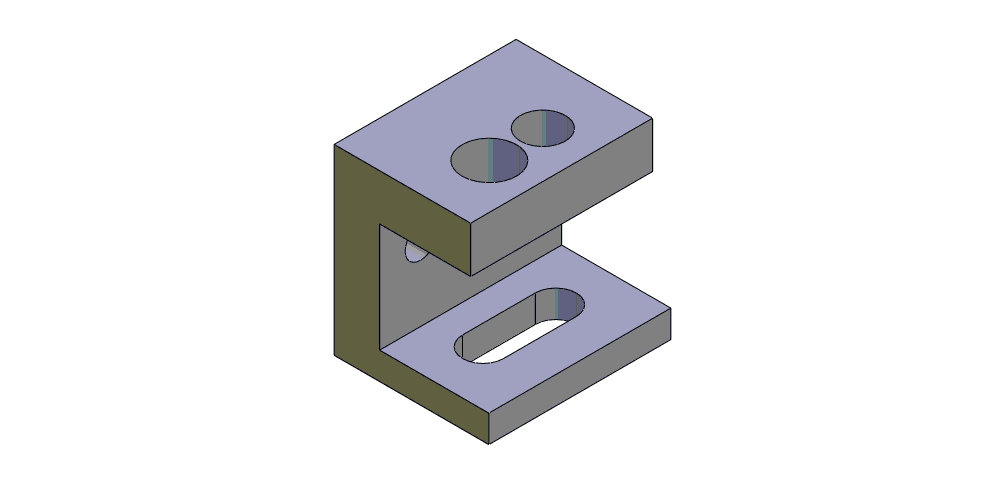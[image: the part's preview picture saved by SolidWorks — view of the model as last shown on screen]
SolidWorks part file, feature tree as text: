
SOLIDWORKS PART (.sldprt)
format: sldprt  version: not decoded by parser v0  size: 209,920 bytes
history: native  units: mm
features: sketch x8, extrude x3, cut_extrude x3, material x1, hole x1 (+12 scaffold rows collapsed)
feature tree (28):
  scaffold x12  (default folders/planes/origin — collapsed)
  material  "Material <not specified>"
  sketch  "Sketch1"  dims[D1=20.0mm D2=15.0mm]
  extrude  "Boss-Extrude1"  Depth=5.08mm
  sketch  "Sketch2"  dims[D1=5.0mm]
  extrude  "Boss-Extrude2"  Depth=15mm
  sketch  "Sketch3"  dims[D1=7.0mm]
  sketch  "Sketch4"  dims[D1=6.0mm]
  hole  "M3 Clearance Hole1"  Diameter=3.4mm Depth=5mm
  sketch  "Sketch6"  dims[D1=4.5mm D2=4.5mm D3=4.0mm D4=4.0mm]
  sketch  "Sketch5"  dims[hole-wizard template sketch: 61 standard entries collapsed; hole parameters above]
  sketch  "Sketch7"  dims[D1=3.0mm]
  extrude  "Boss-Extrude3"  Depth=12mm
  cut_extrude  "Cut-Extrude1"  Depth=12mm
  cut_extrude  "Cut-Extrude2"  Depth=12mm
  sketch  "Sketch8"  dims[D1=6.0mm D2=6.0mm D3=4.5mm]
  cut_extrude  "Cut-Extrude3"  Depth=12mm
decode coverage: 15 of 15 modeling features carry decoded parameters
note: ~ marks probable driven/reference dimensions
note: suppression state not decoded; provenance and decode notes live in map.json
